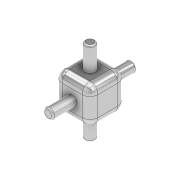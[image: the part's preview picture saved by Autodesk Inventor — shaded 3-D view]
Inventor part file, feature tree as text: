
AUTODESK INVENTOR PART (.ipt)
format: ipt  version: 2020 (Build 240168000, 168)  size: 175,104 bytes
history: native  units: in
note: dims shown in document units (in); Inventor stores cm internally (conversion verified against a paired STEP export)
features: sketch x7, extrude x6, fillet x2, plane x1, revolve x1
ambient origin geometry x8: Origin, YZ Plane, XZ Plane, XY Plane, X Axis, Y Axis, Z Axis, Center Point
bodies: Solid1 (feature_tree)
feature tree (17):
  extrude  "Extrusion1"  Depth=0.1772in
  extrude  "Extrusion2"  Depth=0.1772in
  extrude  "Extrusion3"  Depth=0.1181in TaperAngle=0.0deg
  extrude  "Extrusion4"  Depth=0.1181in TaperAngle=0.0deg
  extrude  "Extrusion5"  Depth=0.0079in
  fillet  "Fillet1"  [1 undecoded]
  fillet  "Fillet2"  Radius=0.0394in
  plane  "Work Plane1"
  revolve  "Revolution1"  [1 undecoded]
  extrude  "Extrusion7"  [1 undecoded]
  sketch  "Sketch1"  dims[d0=0.1772in d1=0.1772in]
  sketch  "Sketch2"  dims[d2=0.1772in d3=0.0in d4=0.0492in]
  sketch  "Sketch3"  dims[d5=0.1181in d6=0.0in d7=0.1181in d8=0.0in]
  sketch  "Sketch4"  dims[d9=0.1181in d10=0.0in d11=0.1181in d12=0.0in]
  sketch  "Sketch5"  dims[d13=0.0394in d14=0.0079in d18=-0.0886in d19=0.0394in]
  sketch  "Sketch8"  dims[d20=90.0deg d21=0.1181in d22=0.0in]
  sketch  "Sketch9"
note: 3 required parameter values undecoded (feature->parameter linkage not recoverable at this tier; creation-order binding heuristic only, values carry confidence <= 0.55)